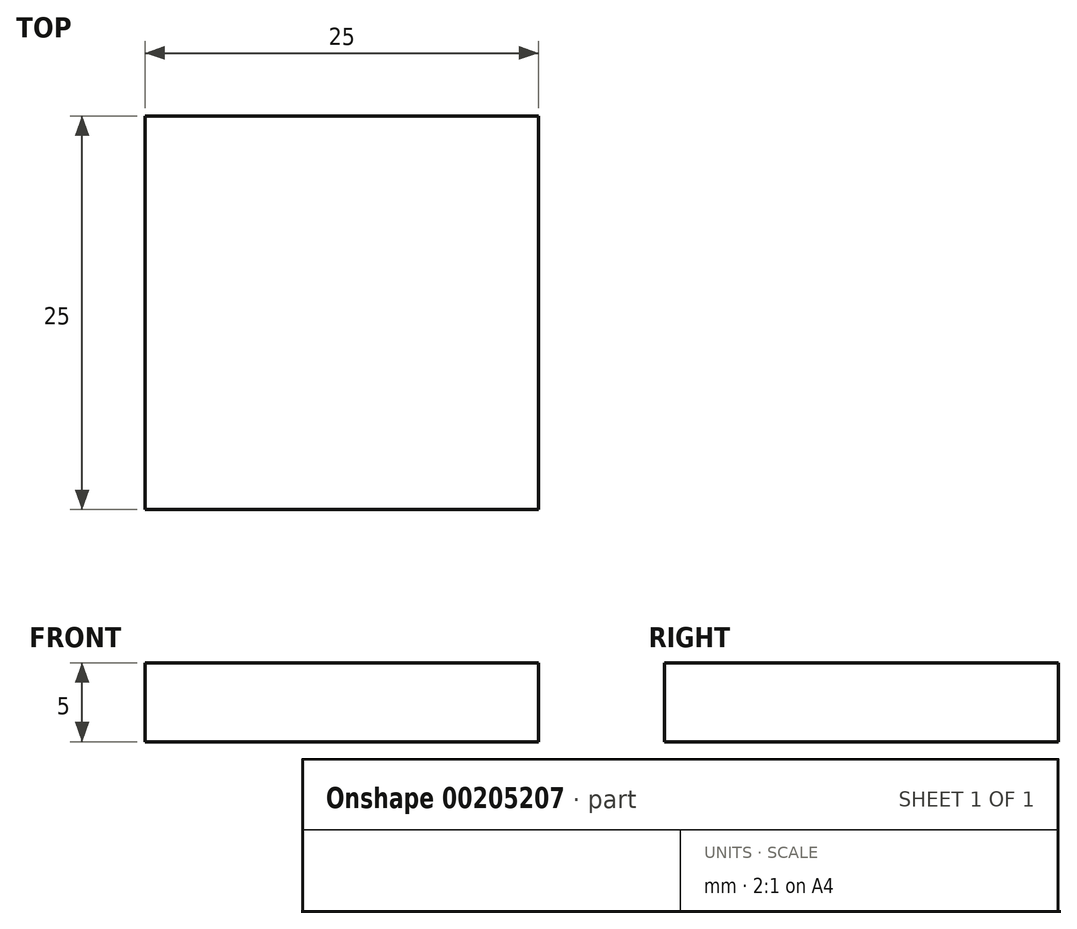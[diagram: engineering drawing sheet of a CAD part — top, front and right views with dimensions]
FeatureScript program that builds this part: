
annotation { "Feature Type Name" : "Feature", "Feature Type Description" : "" }
export const myFeature = defineFeature(function(context is Context, id is Id, definition is map)
    precondition{}
    {
        {
            var Q0;
            Q0=qCreatedBy(makeId("Top.planeOp"),FACE);
            var sketch = newSketch(context, id + "F0", { "sketchPlane" : qUnion([Q0])});
            skLineSegment(sketch, "E0.bottom", {"start": v(0, 0) * mm, "end": v(25, 0) * mm});
            skLineSegment(sketch, "E0.top", {"start": v(0, 25) * mm, "end": v(25, 25) * mm});
            skLineSegment(sketch, "E0.left", {"start": v(0, 0) * mm, "end": v(0, 25) * mm});
            skLineSegment(sketch, "E0.right", {"start": v(25, 0) * mm, "end": v(25, 25) * mm});
            skSolve(sketch);
        }
        {
            var Q0;
            Q0=makeQuery(id+"F0.imprint","IMPRINT",FACE,{"disambiguationData":[TD([[makeQuery(id+"F0.imprint","IMPRINT",EDGE,{"derivedFrom":sQuery(id+"F0.wireOp",EDGE,"E0.bottom")}),1.0]])]});
            extrude(context, id + "F1", {"entities" : qUnion([Q0]), "depth" : 5 * mm});
        }
    });
